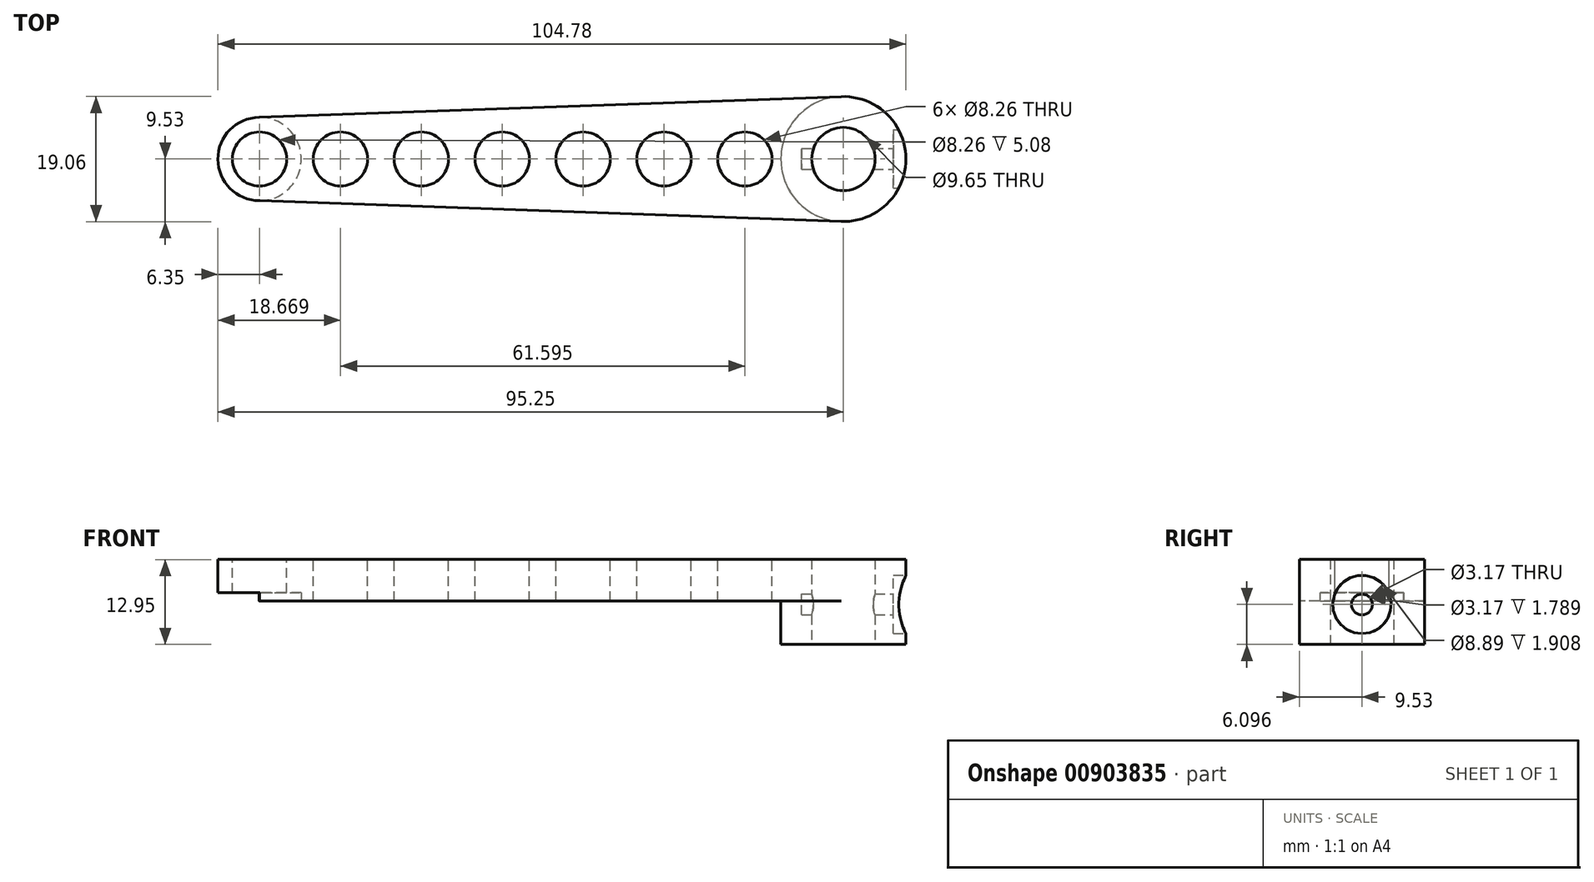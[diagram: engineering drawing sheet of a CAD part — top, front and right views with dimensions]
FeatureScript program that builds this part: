
annotation { "Feature Type Name" : "Feature", "Feature Type Description" : "" }
export const myFeature = defineFeature(function(context is Context, id is Id, definition is map)
    precondition{}
    {
        {
            var Q0;
            Q0=qCreatedBy(makeId("Top.planeOp"),FACE);
            var sketch = newSketch(context, id + "F0", { "sketchPlane" : qUnion([Q0])});
            skCircle(sketch, "E0", {"center": v(0, 0) * mm, "radius": 4.83 * mm});
            skCircle(sketch, "E1", {"center": v(0, 0) * mm, "radius": 9.53 * mm});
            skSolve(sketch);
        }
        {
            var Q0;
            Q0=makeQuery(id+"F0.imprint","IMPRINT",FACE,{"disambiguationData":[TD([[makeQuery(id+"F0.imprint","IMPRINT",EDGE,{"derivedFrom":sQuery(id+"F0.wireOp",EDGE,"E0")}),-1.0]])]});
            extrude(context, id + "F1", {"entities" : qUnion([Q0]), "depth" : 12.95 * mm, "offsetDistance" : 25.4 * mm});
        }
        {
            var Q0;
            Q0=makeQuery(id+"F1.opExtrude","CAP_FACE",FACE,{"disambiguationData":[OSD([sQuery(id+"F0.wireOp",EDGE,"E0"),sQuery(id+"F0.wireOp",EDGE,"E1")])],"isStart":false});
            var sketch = newSketch(context, id + "F2", { "sketchPlane" : qUnion([Q0])});
            skCircle(sketch, "E2", {"center": v(0, 0) * mm, "radius": 9.53 * mm});
            skCircle(sketch, "E3", {"center": v(-88.9, 0) * mm, "radius": 6.35 * mm});
            skLineSegment(sketch, "E4", {"start": v(-88.97, 6.35) * mm, "end": v(0, 9.53) * mm});
            skLineSegment(sketch, "E5", {"start": v(-88.9, -6.35) * mm, "end": v(0, -9.53) * mm});
            skCircle(sketch, "E6", {"center": v(-88.9, 0) * mm, "radius": 4.13 * mm});
            skCircle(sketch, "E7.1.0.0", {"center": v(-76.58, 0) * mm, "radius": 4.13 * mm});
            skCircle(sketch, "E7.2.0.0", {"center": v(-64.26, 0) * mm, "radius": 4.13 * mm});
            skCircle(sketch, "E7.3.0.0", {"center": v(-51.94, 0) * mm, "radius": 4.13 * mm});
            skCircle(sketch, "E7.4.0.0", {"center": v(-39.62, 0) * mm, "radius": 4.13 * mm});
            skLineSegment(sketch, "E7.direction1", {"start": v(-88.9, 0) * mm, "end": v(-76.58, 0) * mm, "construction": true});
            skCircle(sketch, "E8.0.5.0", {"center": v(-27.3, 0) * mm, "radius": 4.13 * mm});
            skCircle(sketch, "E9.0.6.0", {"center": v(-14.99, 0) * mm, "radius": 4.13 * mm});
            skSolve(sketch);
        }
        {
            var Q0;
            Q0 = qSketchRegion(id + "F2", true);
            extrude(context, id + "F3", {"entities" : qUnion([Q0]), "operationType" : NewBodyOperationType.ADD, "oppositeDirection" : true, "depth" : 6.35 * mm, "offsetDistance" : 25.4 * mm});
        }
        {
            var Q0;
            Q0=qCreatedBy(makeId("Right.planeOp"),FACE);
            cPlane(context, id + "F4", {"entities" : qUnion([Q0]), "cplaneType" : CPlaneType.OFFSET, "offset" : 25.4 * mm, "width" : 152.4 * mm, "height" : 152.4 * mm});
        }
        {
            var Q0;
            Q0=qCreatedBy(id+"F4.planeOp",FACE);
            var sketch = newSketch(context, id + "F5", { "sketchPlane" : qUnion([Q0])});
            skLineSegment(sketch, "E10", {"start": v(0, 0) * mm, "end": v(0, 6.1) * mm, "construction": true});
            skCircle(sketch, "E11", {"center": v(0, 6.1) * mm, "radius": 1.59 * mm});
            skCircle(sketch, "E12", {"center": v(0, 6.1) * mm, "radius": 4.45 * mm});
            skSolve(sketch);
        }
        {
            var Q0;
            Q0=makeQuery(id+"F5.imprint","IMPRINT",FACE,{"disambiguationData":[TD([[makeQuery(id+"F5.imprint","IMPRINT",EDGE,{"derivedFrom":sQuery(id+"F5.wireOp",EDGE,"E11")}),1.0]])]});
            extrude(context, id + "F6", {"entities" : qUnion([Q0]), "operationType" : NewBodyOperationType.REMOVE, "oppositeDirection" : true, "depth" : 31.75 * mm, "offsetDistance" : 25.4 * mm});
        }
        {
            var Q0;
            Q0=makeQuery(id+"F0.imprint","IMPRINT",FACE,{"disambiguationData":[TD([[makeQuery(id+"F0.imprint","IMPRINT",EDGE,{"derivedFrom":sQuery(id+"F0.wireOp",EDGE,"E0")}),1.0]])]});
            extrude(context, id + "F7", {"entities" : qUnion([Q0]), "operationType" : NewBodyOperationType.REMOVE, "depth" : 25.4 * mm, "offsetDistance" : 25.4 * mm});
        }
        {
            var Q0;
            {var subQ0=sQuery(id+"F2.wireOp",EDGE,"E7.4.0.0");var subQ1=sQuery(id+"F2.wireOp",EDGE,"E7.3.0.0");var subQ2=sQuery(id+"F2.wireOp",EDGE,"E7.1.0.0");var subQ3=sQuery(id+"F2.wireOp",EDGE,"E6");var subQ4=sQuery(id+"F2.wireOp",EDGE,"pdIjIbcP-9SOD-l8nC-nuJ8-Q8D78OAUkfvr");var subQ5=sQuery(id+"F2.wireOp",EDGE,"E7.2.0.0");var subQ6=sQuery(id+"F2.wireOp",EDGE,"E4");var subQ7=sQuery(id+"F2.wireOp",EDGE,"E3");var subQ8=sQuery(id+"F2.wireOp",EDGE,"E5");var subQ9=sQuery(id+"F2.wireOp",EDGE,"E8.0.5.0");Q0=makeQuery(id+"F3.boolean.opBoolean","SPLIT",FACE,{"disambiguationData":[TD([makeQuery(id+"F1.opExtrude","SWEPT_FACE",FACE,{"disambiguationData":[OSD([sQuery(id+"F0.wireOp",EDGE,"E1")])]})])],"derivedFrom":makeQuery(id+"F3.opExtrude","CAP_FACE",FACE,{"disambiguationData":[OSD([sQuery(id+"F2.wireOp",EDGE,"E2"),subQ7,subQ6,subQ8,subQ4,subQ3,subQ2,subQ5,subQ1,subQ0,subQ9])],"isStart":false})});}
            var sketch = newSketch(context, id + "F8", { "sketchPlane" : qUnion([Q0])});
            skCircle(sketch, "E13", {"center": v(-88.9, 0) * mm, "radius": 6.35 * mm});
            skSolve(sketch);
        }
        {
            var Q0;
            Q0 = qSketchRegion(id + "F8", true);
            extrude(context, id + "F9", {"entities" : qUnion([Q0]), "operationType" : NewBodyOperationType.REMOVE, "oppositeDirection" : true, "depth" : 1.27 * mm, "offsetDistance" : 25.4 * mm});
        }
        {
            var Q0;
            Q0=makeQuery(id+"F5.imprint","IMPRINT",FACE,{"disambiguationData":[TD([[makeQuery(id+"F5.imprint","IMPRINT",EDGE,{"derivedFrom":sQuery(id+"F5.wireOp",EDGE,"E11")}),-1.0]])]});
            extrude(context, id + "F10", {"entities" : qUnion([Q0]), "operationType" : NewBodyOperationType.REMOVE, "oppositeDirection" : true, "depth" : 17.78 * mm, "offsetDistance" : 25.4 * mm});
        }
        {
            var Q0;
            {var subQ0=sQuery(id+"F2.wireOp",EDGE,"E5");Q0=makeQuery(id+"F9.boolean.opBoolean","SPLIT",EDGE,{"disambiguationData":[topologyDisambiguationEdgeConnected([makeQuery(id+"F9.opExtrude","SWEPT_FACE",FACE,{"disambiguationData":[OSD([sQuery(id+"F8.wireOp",EDGE,"E13")])]})])],"derivedFrom":makeQuery(id+"F3.opExtrude","SWEPT_EDGE",EDGE,{"disambiguationData":[OSD([sQuery(id+"F2.wireOp",EDGE,"E3"),subQ0])]})});}
            var Q1;
            {var subQ0=sQuery(id+"F2.wireOp",EDGE,"E4");Q1=makeQuery(id+"F9.boolean.opBoolean","SPLIT",EDGE,{"disambiguationData":[topologyDisambiguationEdgeConnected([makeQuery(id+"F9.opExtrude","SWEPT_FACE",FACE,{"disambiguationData":[OSD([sQuery(id+"F8.wireOp",EDGE,"E13")])]})])],"derivedFrom":makeQuery(id+"F3.opExtrude","SWEPT_EDGE",EDGE,{"disambiguationData":[OSD([sQuery(id+"F2.wireOp",EDGE,"E3"),subQ0])]})});}
            fillet(context, id + "F11", {"entities" : qUnion([Q0, Q1]), "tangentPropagation" : true, "radius" : 2.54 * mm, "defaultsChanged" : true, "vertexSettings" : [], "allowEdgeOverflow" : false});
        }
    });
